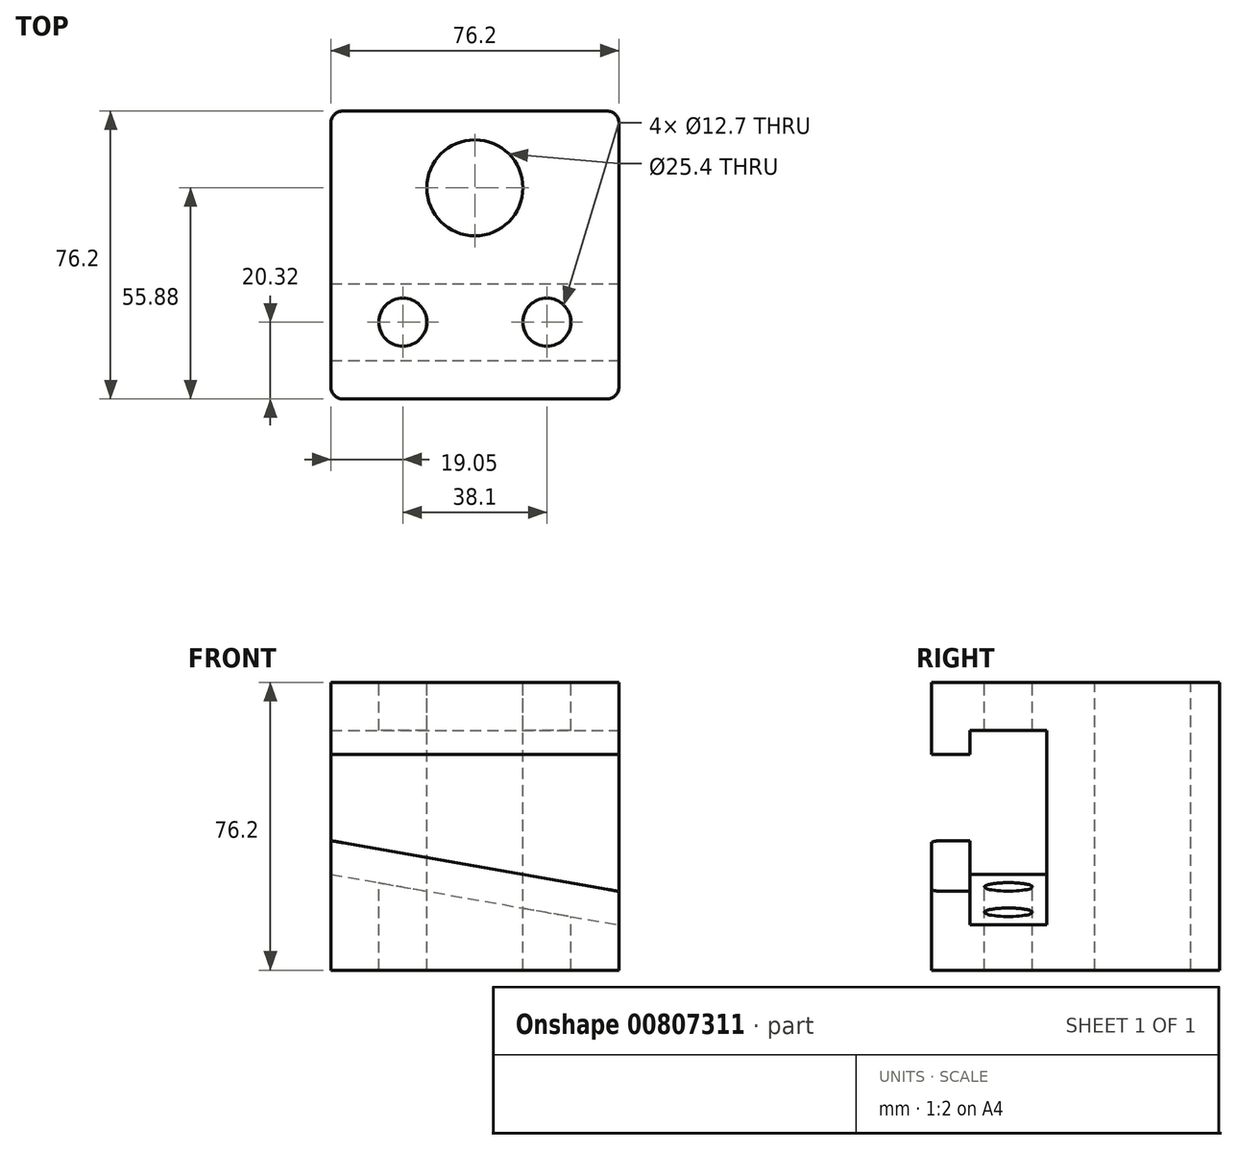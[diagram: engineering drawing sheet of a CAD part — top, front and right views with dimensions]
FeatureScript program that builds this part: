
annotation { "Feature Type Name" : "Feature", "Feature Type Description" : "" }
export const myFeature = defineFeature(function(context is Context, id is Id, definition is map)
    precondition{}
    {
        {
            var Q0;
            Q0=qCreatedBy(makeId("Front.planeOp"),FACE);
            var sketch = newSketch(context, id + "F0", { "sketchPlane" : qUnion([Q0])});
            skLineSegment(sketch, "E0.bottom", {"start": v(0, 0) * mm, "end": v(76.2, 0) * mm});
            skLineSegment(sketch, "E0.top", {"start": v(0, 76.2) * mm, "end": v(76.2, 76.2) * mm});
            skLineSegment(sketch, "E0.left", {"start": v(0, 0) * mm, "end": v(0, 76.2) * mm});
            skLineSegment(sketch, "E0.right", {"start": v(76.2, 0) * mm, "end": v(76.2, 76.2) * mm});
            skLineSegment(sketch, "E1", {"start": v(0, 63.5) * mm, "end": v(76.2, 63.5) * mm});
            skLineSegment(sketch, "E2", {"start": v(0, 57.15) * mm, "end": v(76.2, 57.15) * mm});
            skLineSegment(sketch, "E3", {"start": v(0, 25.4) * mm, "end": v(76.2, 11.96) * mm});
            skLineSegment(sketch, "E4", {"start": v(0, 34.3) * mm, "end": v(76.2, 20.85) * mm});
            skSolve(sketch);
        }
        {
            var Q0;
            {var subQ0=sQuery(id+"F0.wireOp",EDGE,"E0.top");Q0=makeQuery(id+"F0.imprint","IMPRINT",FACE,{"disambiguationData":[TD([[makeQuery(id+"F0.imprint","IMPRINT",EDGE,{"derivedFrom":subQ0}),-1.0]])]});}
            var Q1;
            {var subQ0=sQuery(id+"F0.wireOp",EDGE,"E1");Q1=makeQuery(id+"F0.imprint","IMPRINT",FACE,{"disambiguationData":[TD([[makeQuery(id+"F0.imprint","IMPRINT",EDGE,{"derivedFrom":subQ0}),-1.0]])]});}
            var Q2;
            {var subQ0=sQuery(id+"F0.wireOp",EDGE,"E2");Q2=makeQuery(id+"F0.imprint","IMPRINT",FACE,{"disambiguationData":[TD([[makeQuery(id+"F0.imprint","IMPRINT",EDGE,{"derivedFrom":subQ0}),-1.0]])]});}
            var Q3;
            {var subQ0=sQuery(id+"F0.wireOp",EDGE,"E3");Q3=makeQuery(id+"F0.imprint","IMPRINT",FACE,{"disambiguationData":[TD([[makeQuery(id+"F0.imprint","IMPRINT",EDGE,{"derivedFrom":subQ0}),1.0]])]});}
            var Q4;
            {var subQ0=sQuery(id+"F0.wireOp",EDGE,"E0.bottom");Q4=makeQuery(id+"F0.imprint","IMPRINT",FACE,{"disambiguationData":[TD([[makeQuery(id+"F0.imprint","IMPRINT",EDGE,{"derivedFrom":subQ0}),1.0]])]});}
            extrude(context, id + "F1", {"entities" : qUnion([Q0, Q1, Q2, Q3, Q4]), "oppositeDirection" : true, "depth" : 45.72 * mm, "offsetDistance" : 25.4 * mm});
        }
        {
            var Q0;
            {var subQ0=sQuery(id+"F0.wireOp",EDGE,"E0.top");Q0=makeQuery(id+"F0.imprint","IMPRINT",FACE,{"disambiguationData":[TD([[makeQuery(id+"F0.imprint","IMPRINT",EDGE,{"derivedFrom":subQ0}),-1.0]])]});}
            var Q1;
            {var subQ0=sQuery(id+"F0.wireOp",EDGE,"E0.bottom");Q1=makeQuery(id+"F0.imprint","IMPRINT",FACE,{"disambiguationData":[TD([[makeQuery(id+"F0.imprint","IMPRINT",EDGE,{"derivedFrom":subQ0}),1.0]])]});}
            extrude(context, id + "F2", {"entities" : qUnion([Q0, Q1]), "operationType" : NewBodyOperationType.ADD, "depth" : 20.32 * mm, "offsetDistance" : 25.4 * mm});
        }
        {
            var Q0;
            Q0=makeQuery(id+"F2.opExtrude","CAP_FACE",FACE,{"disambiguationData":[OSD([sQuery(id+"F0.wireOp",EDGE,"E0.top"),sQuery(id+"F0.wireOp",EDGE,"E0.left"),sQuery(id+"F0.wireOp",EDGE,"E0.right"),sQuery(id+"F0.wireOp",EDGE,"E1")])],"isStart":false});
            var sketch = newSketch(context, id + "F3", { "sketchPlane" : qUnion([Q0])});
            skLineSegment(sketch, "E5.0", {"start": v(0, 76.2) * mm, "end": v(76.2, 76.2) * mm});
            skLineSegment(sketch, "E6.0", {"start": v(0, 57.15) * mm, "end": v(76.2, 57.15) * mm});
            skLineSegment(sketch, "E7.0", {"start": v(0, 34.3) * mm, "end": v(76.2, 20.85) * mm});
            skLineSegment(sketch, "E8.0", {"start": v(0, 0) * mm, "end": v(76.2, 0) * mm});
            skLineSegment(sketch, "E9", {"start": v(0, 76.2) * mm, "end": v(0, 57.15) * mm});
            skLineSegment(sketch, "E10", {"start": v(76.2, 76.2) * mm, "end": v(76.2, 57.15) * mm});
            skLineSegment(sketch, "E11", {"start": v(76.2, 20.85) * mm, "end": v(76.2, 0) * mm});
            skLineSegment(sketch, "E12", {"start": v(0, 0) * mm, "end": v(0, 34.3) * mm});
            skSolve(sketch);
        }
        {
            var Q0;
            {var subQ0=sQuery(id+"F3.wireOp",EDGE,"E5.0");Q0=makeQuery(id+"F3.imprint","IMPRINT",FACE,{"disambiguationData":[TD([[makeQuery(id+"F3.imprint","IMPRINT",EDGE,{"derivedFrom":subQ0}),-1.0]])]});}
            var Q1;
            {var subQ0=sQuery(id+"F3.wireOp",EDGE,"E6.0");Q1=makeQuery(id+"F3.imprint","IMPRINT",FACE,{"disambiguationData":[TD([[makeQuery(id+"F3.imprint","IMPRINT",EDGE,{"derivedFrom":subQ0}),1.0]])]});}
            var Q2;
            Q2=makeQuery(id+"F3.imprint","IMPRINT",FACE,{"disambiguationData":[TD([[makeQuery(id+"F3.imprint","IMPRINT",EDGE,{"derivedFrom":sQuery(id+"F3.wireOp",EDGE,"E7.0")}),-1.0]])]});
            extrude(context, id + "F4", {"entities" : qUnion([Q0, Q1, Q2]), "operationType" : NewBodyOperationType.ADD, "depth" : 10.16 * mm, "offsetDistance" : 25.4 * mm});
        }
        {
            var Q0;
            {var subQ0=sQuery(id+"F0.wireOp",EDGE,"E0.top");Q0=makeQuery(id+"F4.boolean.opBoolean","MERGE",FACE,{"derivedFrom":[makeQuery(id+"F2.boolean.opBoolean","MERGE",FACE,{"derivedFrom":[makeQuery(id+"F1.opExtrude","SWEPT_FACE",FACE,{"disambiguationData":[OSD([subQ0])]}),makeQuery(id+"F2.opExtrude","SWEPT_FACE",FACE,{"disambiguationData":[OSD([subQ0])]})]}),makeQuery(id+"F4.opExtrude","SWEPT_FACE",FACE,{"disambiguationData":[OSD([sQuery(id+"F3.wireOp",EDGE,"E5.0")])]})]});}
            var sketch = newSketch(context, id + "F5", { "sketchPlane" : qUnion([Q0])});
            skLineSegment(sketch, "E13.0", {"start": v(0, 45.72) * mm, "end": v(0, -30.48) * mm});
            skLineSegment(sketch, "E14.0", {"start": v(0, -30.48) * mm, "end": v(76.2, -30.48) * mm});
            skLineSegment(sketch, "E15.0", {"start": v(76.2, 45.72) * mm, "end": v(76.2, -30.48) * mm});
            skLineSegment(sketch, "E16.0", {"start": v(0, 45.72) * mm, "end": v(76.2, 45.72) * mm});
            skCircle(sketch, "E17", {"center": v(38.1, 25.4) * mm, "radius": 12.7 * mm});
            skCircle(sketch, "E18", {"center": v(57.15, -10.16) * mm, "radius": 6.35 * mm});
            skCircle(sketch, "E19", {"center": v(19.05, -10.16) * mm, "radius": 6.35 * mm});
            skSolve(sketch);
        }
        {
            var Q0;
            Q0=makeQuery(id+"F5.imprint","IMPRINT",FACE,{"disambiguationData":[TD([[makeQuery(id+"F5.imprint","IMPRINT",EDGE,{"derivedFrom":sQuery(id+"F5.wireOp",EDGE,"E19")}),1.0]])]});
            var Q1;
            Q1=makeQuery(id+"F5.imprint","IMPRINT",FACE,{"disambiguationData":[TD([[makeQuery(id+"F5.imprint","IMPRINT",EDGE,{"derivedFrom":sQuery(id+"F5.wireOp",EDGE,"E18")}),1.0]])]});
            var Q2;
            Q2=makeQuery(id+"F5.imprint","IMPRINT",FACE,{"disambiguationData":[TD([[makeQuery(id+"F5.imprint","IMPRINT",EDGE,{"derivedFrom":sQuery(id+"F5.wireOp",EDGE,"E17")}),1.0]])]});
            extrude(context, id + "F6", {"entities" : qUnion([Q0, Q1, Q2]), "operationType" : NewBodyOperationType.REMOVE, "endBound" : BoundingType.THROUGH_ALL, "oppositeDirection" : true, "depth" : 25.4 * mm, "offsetDistance" : 25.4 * mm});
        }
        {
            var Q0;
            Q0=makeQuery(id+"F4.opExtrude","CAP_EDGE",EDGE,{"disambiguationData":[OSD([sQuery(id+"F3.wireOp",EDGE,"E11")])],"isStart":false});
            var Q1;
            Q1=makeQuery(id+"F4.opExtrude","CAP_EDGE",EDGE,{"disambiguationData":[OSD([sQuery(id+"F3.wireOp",EDGE,"E12")])],"isStart":false});
            var Q2;
            Q2=makeQuery(id+"F1.opExtrude","CAP_EDGE",EDGE,{"disambiguationData":[OSD([sQuery(id+"F0.wireOp",EDGE,"E0.right")])],"isStart":false});
            var Q3;
            Q3=makeQuery(id+"F1.opExtrude","CAP_EDGE",EDGE,{"disambiguationData":[OSD([sQuery(id+"F0.wireOp",EDGE,"E0.left")])],"isStart":false});
            var Q4;
            Q4=makeQuery(id+"F4.opExtrude","CAP_EDGE",EDGE,{"disambiguationData":[OSD([sQuery(id+"F3.wireOp",EDGE,"E10")])],"isStart":false});
            var Q5;
            Q5=makeQuery(id+"F4.opExtrude","CAP_EDGE",EDGE,{"disambiguationData":[OSD([sQuery(id+"F3.wireOp",EDGE,"E9")])],"isStart":false});
            fillet(context, id + "F7", {"entities" : qUnion([Q0, Q1, Q2, Q3, Q4, Q5]), "radius" : 3.17 * mm, "tangentPropagation" : true, "allowEdgeOverflow" : false});
        }
    });
